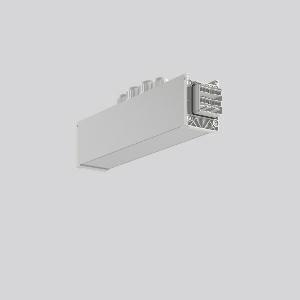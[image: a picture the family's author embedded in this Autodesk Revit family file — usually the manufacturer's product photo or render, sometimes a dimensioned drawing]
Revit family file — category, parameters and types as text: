
# Revit family: linedo_mitteleinspeisung_14pol_982698_000_2bfd
name_source: partatom
category: Lighting Fixtures
units: mm (PartAtom-declared; Revit-internal decimal feet)

## family parameters
Cut with Voids When Loaded = No
Host = Face
Light Source = No
Part Type = Normal
Room Calculation Point = No
Round Connector Dimension = Use Diameter
Shared = No

## types (1)
- LINEDO_Mitteleinspeisung_14pol
    Apparent Load = 0 VA
    Default Elevation = 1800 mm
    Description = Series: LINEDO
Middle power feed, 14-pole, connection socket / plug. Housing: extruded aluminium profile, anodised. Cover made of plastic, surface like housing. LINEDO plug system, plastic, light grey. 4 cable glands (2 x M20 and 2 x M25). Cable glands on top. Easy connection for rigid or flexible wires.
Colour: anodised aluminium
Length: 330 mm
Width: 58 mm
Height: 76 mm
Weight: 850 g
    Height = 76 mm
    Lamp = 0 x
    Length = 330 mm
    Luminous efficacy = 0 lm/W
    Manufacturer = RZB
    ModVariant = No
    Model = 982698.000
    Mounting Place = Ceiling
    Mounting Type = Surface mounted, Pendant
    Number of Poles = 1
    OnlyDefault = Yes
    Power Factor = 1
    Product Name = LINEDO_Mitteleinspeisung_14pol
    Product group = Surface mounted continuous line luminaire system
    ProductGroupID = 310
    Protection Class = Protection class I
    Protection Degree = IP 54
    RLX_Detail_Level = 1
    RLX_Emergency_Light_Flux = 0 lm
    RLX_Emergency_Type = 0
    RLX_Emergency_Type_DB = No
    RlxData = <blob elided: 21849 chars, md5=7e0aac91>
    Standby Power = 0 W
    System Light Flux = 0 lm
    System Power = 0 W
    Type Comments = Product without accessories
    Type Image = 982698.000.jpg
    URL = http://relux.com
    VarID = ---
    Voltage = 0 V
    Weight = 0.00 kg
    Width = 58 mm

## geometry (parser evidence)
native form markers: Blend x4, Sweep x12
no freeform markers — native parametric forms only
